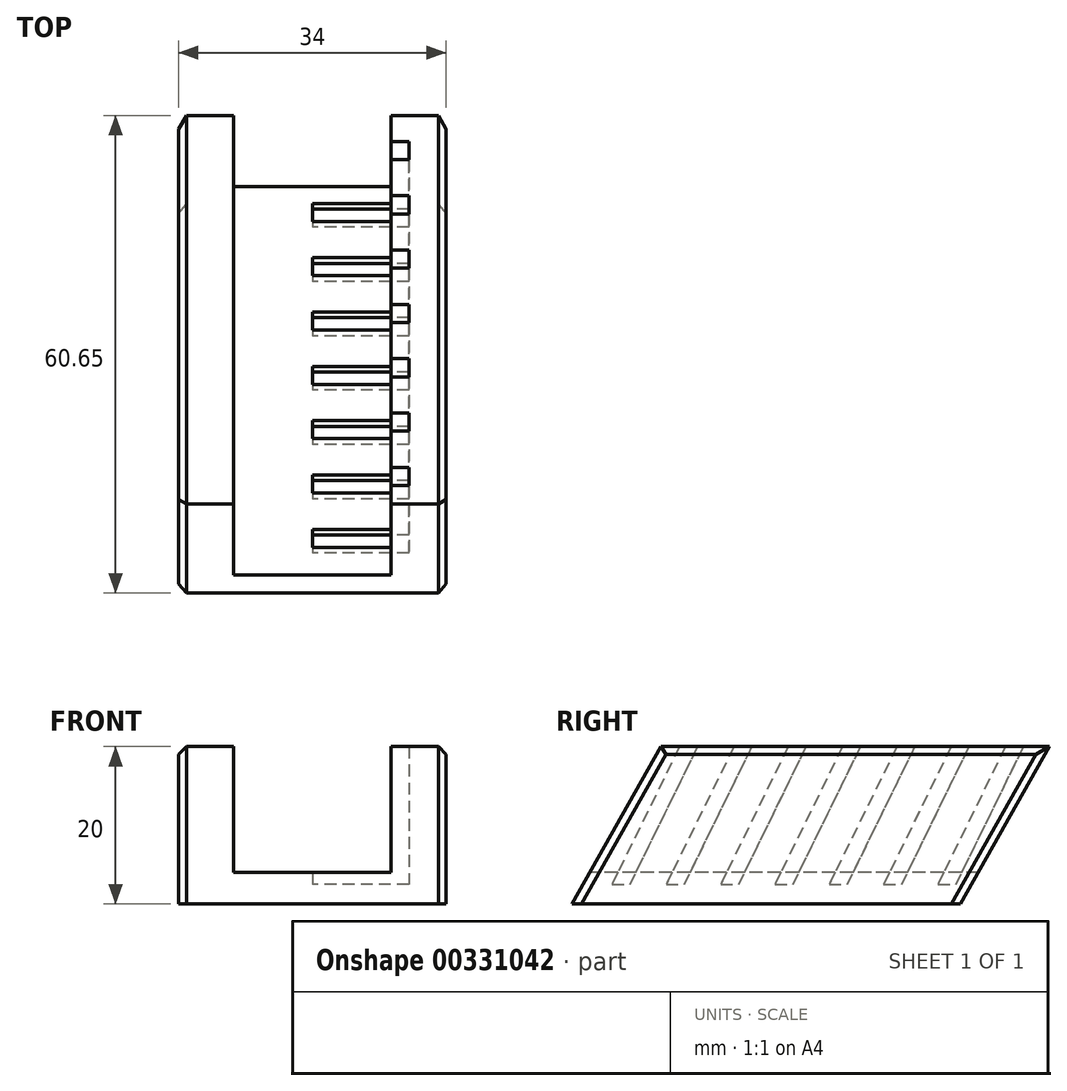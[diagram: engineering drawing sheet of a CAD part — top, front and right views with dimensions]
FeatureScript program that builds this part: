
annotation { "Feature Type Name" : "Feature", "Feature Type Description" : "" }
export const myFeature = defineFeature(function(context is Context, id is Id, definition is map)
    precondition{}
    {
        {
            var Q0;
            Q0=qCreatedBy(makeId("Right.planeOp"),FACE);
            var sketch = newSketch(context, id + "F0", { "sketchPlane" : qUnion([Q0])});
            skLineSegment(sketch, "E0", {"start": v(-26.1, 3.5) * mm, "end": v(-37.4, -16.5) * mm});
            skLineSegment(sketch, "E1", {"start": v(-37.4, -16.5) * mm, "end": v(11.94, -16.5) * mm});
            skLineSegment(sketch, "E2", {"start": v(11.94, -16.5) * mm, "end": v(23.24, 3.5) * mm});
            skLineSegment(sketch, "E3", {"start": v(23.24, 3.5) * mm, "end": v(-26.1, 3.5) * mm});
            skSolve(sketch);
        }
        {
            var Q0;
            Q0=makeQuery(id+"F0.imprint","IMPRINT",FACE,{"disambiguationData":[TD([[makeQuery(id+"F0.imprint","IMPRINT",EDGE,{"derivedFrom":sQuery(id+"F0.wireOp",EDGE,"E0")}),1.0]])]});
            extrude(context, id + "F1", {"entities" : qUnion([Q0]), "depth" : 17 * mm});
        }
        {
            var Q0;
            Q0=makeQuery(id+"F1.opExtrude","SWEPT_BODY",BODY,{"disambiguationData":[OSD([sQuery(id+"F0.wireOp",EDGE,"E0"),sQuery(id+"F0.wireOp",EDGE,"E1"),sQuery(id+"F0.wireOp",EDGE,"E2"),sQuery(id+"F0.wireOp",EDGE,"E3")])]});
            var Q1;
            Q1=makeQuery(id+"F1.opExtrude","CAP_FACE",FACE,{"disambiguationData":[OSD([sQuery(id+"F0.wireOp",EDGE,"E0"),sQuery(id+"F0.wireOp",EDGE,"E1"),sQuery(id+"F0.wireOp",EDGE,"E2"),sQuery(id+"F0.wireOp",EDGE,"E3")])],"isStart":true});
            mirror(context, id + "F2", {"operationType" : NewBodyOperationType.ADD, "entities" : qUnion([Q0]), "mirrorPlane" : qUnion([Q1])});
        }
        {
            var Q0;
            Q0=qCreatedBy(makeId("Right.planeOp"),FACE);
            var sketch = newSketch(context, id + "F3", { "sketchPlane" : qUnion([Q0])});
            skLineSegment(sketch, "E4", {"start": v(-22.2, 6.68) * mm, "end": v(-32.34, -14) * mm});
            skLineSegment(sketch, "E5", {"start": v(-32.34, -14) * mm, "end": v(-30.04, -14) * mm});
            skLineSegment(sketch, "E6", {"start": v(-30.04, -14) * mm, "end": v(-19.9, 6.68) * mm});
            skLineSegment(sketch, "E7", {"start": v(-19.9, 6.68) * mm, "end": v(-22.2, 6.68) * mm});
            skLineSegment(sketch, "E8", {"start": v(-37.45, -16.42) * mm, "end": v(33.96, -16.42) * mm});
            skLineSegment(sketch, "E9.1.0.0", {"start": v(-15.3, 6.68) * mm, "end": v(-25.44, -14) * mm});
            skLineSegment(sketch, "E9.1.0.1", {"start": v(-13, 6.68) * mm, "end": v(-15.3, 6.68) * mm});
            skLineSegment(sketch, "E9.1.0.2", {"start": v(-23.14, -14) * mm, "end": v(-13, 6.68) * mm});
            skLineSegment(sketch, "E9.1.0.3", {"start": v(-25.44, -14) * mm, "end": v(-23.14, -14) * mm});
            skLineSegment(sketch, "E9.2.0.0", {"start": v(-8.4, 6.68) * mm, "end": v(-18.54, -14) * mm});
            skLineSegment(sketch, "E9.2.0.1", {"start": v(-6.1, 6.68) * mm, "end": v(-8.4, 6.68) * mm});
            skLineSegment(sketch, "E9.2.0.2", {"start": v(-16.24, -14) * mm, "end": v(-6.1, 6.68) * mm});
            skLineSegment(sketch, "E9.2.0.3", {"start": v(-18.54, -14) * mm, "end": v(-16.24, -14) * mm});
            skLineSegment(sketch, "E9.3.0.0", {"start": v(-1.5, 6.68) * mm, "end": v(-11.64, -14) * mm});
            skLineSegment(sketch, "E9.3.0.1", {"start": v(0.8, 6.68) * mm, "end": v(-1.5, 6.68) * mm});
            skLineSegment(sketch, "E9.3.0.2", {"start": v(-9.34, -14) * mm, "end": v(0.8, 6.68) * mm});
            skLineSegment(sketch, "E9.3.0.3", {"start": v(-11.64, -14) * mm, "end": v(-9.34, -14) * mm});
            skLineSegment(sketch, "E9.4.0.0", {"start": v(5.4, 6.68) * mm, "end": v(-4.74, -14) * mm});
            skLineSegment(sketch, "E9.4.0.1", {"start": v(7.7, 6.68) * mm, "end": v(5.4, 6.68) * mm});
            skLineSegment(sketch, "E9.4.0.2", {"start": v(-2.44, -14) * mm, "end": v(7.7, 6.68) * mm});
            skLineSegment(sketch, "E9.4.0.3", {"start": v(-4.74, -14) * mm, "end": v(-2.44, -14) * mm});
            skLineSegment(sketch, "E9.5.0.0", {"start": v(12.3, 6.68) * mm, "end": v(2.16, -14) * mm});
            skLineSegment(sketch, "E9.5.0.1", {"start": v(14.6, 6.68) * mm, "end": v(12.3, 6.68) * mm});
            skLineSegment(sketch, "E9.5.0.2", {"start": v(4.46, -14) * mm, "end": v(14.6, 6.68) * mm});
            skLineSegment(sketch, "E9.5.0.3", {"start": v(2.16, -14) * mm, "end": v(4.46, -14) * mm});
            skLineSegment(sketch, "E9.direction1", {"start": v(-32.34, -14) * mm, "end": v(-25.44, -14) * mm, "construction": true});
            skLineSegment(sketch, "E10.0.6.0", {"start": v(19.2, 6.68) * mm, "end": v(9.06, -14) * mm});
            skLineSegment(sketch, "E10.3.6.0", {"start": v(21.5, 6.68) * mm, "end": v(19.2, 6.68) * mm});
            skLineSegment(sketch, "E10.6.6.0", {"start": v(11.36, -14) * mm, "end": v(21.5, 6.68) * mm});
            skLineSegment(sketch, "E10.9.6.0", {"start": v(9.06, -14) * mm, "end": v(11.36, -14) * mm});
            skSolve(sketch);
        }
        {
            var Q0;
            Q0 = qSketchRegion(id + "F3", true);
            var Q1;
            Q1 = qConstructionFilter(qBodyType(qCreatedBy(id + "F3" ,EDGE), BodyType.WIRE), ConstructionObject.NO);
            extrude(context, id + "F4", {"entities" : qUnion([Q0]), "operationType" : NewBodyOperationType.REMOVE, "surfaceEntities" : qUnion([Q1]), "depth" : (24.5 / 2) * mm});
        }
        {
            var Q0;
            Q0=qCreatedBy(makeId("Front.planeOp"),FACE);
            var sketch = newSketch(context, id + "F5", { "sketchPlane" : qUnion([Q0])});
            skLineSegment(sketch, "E11.bottom", {"start": v(10, -12.5) * mm, "end": v(-10, -12.5) * mm});
            skLineSegment(sketch, "E11.top", {"start": v(10, 12.5) * mm, "end": v(-10, 12.5) * mm});
            skLineSegment(sketch, "E11.left", {"start": v(10, -12.5) * mm, "end": v(10, 12.5) * mm});
            skLineSegment(sketch, "E11.right", {"start": v(-10, -12.5) * mm, "end": v(-10, 12.5) * mm});
            skPoint(sketch, "E11.middle", {"position": v(0, 0) * mm});
            skSolve(sketch);
        }
        {
            var Q0;
            Q0=makeQuery(id+"F5.imprint","IMPRINT",FACE,{"disambiguationData":[TD([[makeQuery(id+"F5.imprint","IMPRINT",EDGE,{"derivedFrom":sQuery(id+"F5.wireOp",EDGE,"E11.bottom")}),-1.0]])]});
            extrude(context, id + "F6", {"entities" : qUnion([Q0]), "operationType" : NewBodyOperationType.REMOVE, "endBound" : BoundingType.SYMMETRIC, "oppositeDirection" : true, "depth" : 119 * mm});
        }
        {
            var Q0;
            Q0=makeQuery(id+"F2.opPattern","COPY",EDGE,{"derivedFrom":makeQuery(id+"F1.opExtrude","CAP_EDGE",EDGE,{"disambiguationData":[OSD([sQuery(id+"F0.wireOp",EDGE,"E3")])],"isStart":false}),"instanceName":"1"});
            var Q1;
            Q1=makeQuery(id+"F1.opExtrude","CAP_EDGE",EDGE,{"disambiguationData":[OSD([sQuery(id+"F0.wireOp",EDGE,"E3")])],"isStart":false});
            var Q2;
            Q2=makeQuery(id+"F1.opExtrude","CAP_EDGE",EDGE,{"disambiguationData":[OSD([sQuery(id+"F0.wireOp",EDGE,"E0")])],"isStart":false});
            var Q3;
            Q3=makeQuery(id+"F1.opExtrude","CAP_EDGE",EDGE,{"disambiguationData":[OSD([sQuery(id+"F0.wireOp",EDGE,"E2")])],"isStart":false});
            var Q4;
            Q4=makeQuery(id+"F2.opPattern","COPY",EDGE,{"derivedFrom":makeQuery(id+"F1.opExtrude","CAP_EDGE",EDGE,{"disambiguationData":[OSD([sQuery(id+"F0.wireOp",EDGE,"E2")])],"isStart":false}),"instanceName":"1"});
            var Q5;
            Q5=makeQuery(id+"F2.opPattern","COPY",EDGE,{"derivedFrom":makeQuery(id+"F1.opExtrude","CAP_EDGE",EDGE,{"disambiguationData":[OSD([sQuery(id+"F0.wireOp",EDGE,"E0")])],"isStart":false}),"instanceName":"1"});
            chamfer(context, id + "F7", {"entities" : qUnion([Q0, Q1, Q2, Q3, Q4, Q5]), "width" : 1 * mm, "tangentPropagation" : true});
        }
    });
